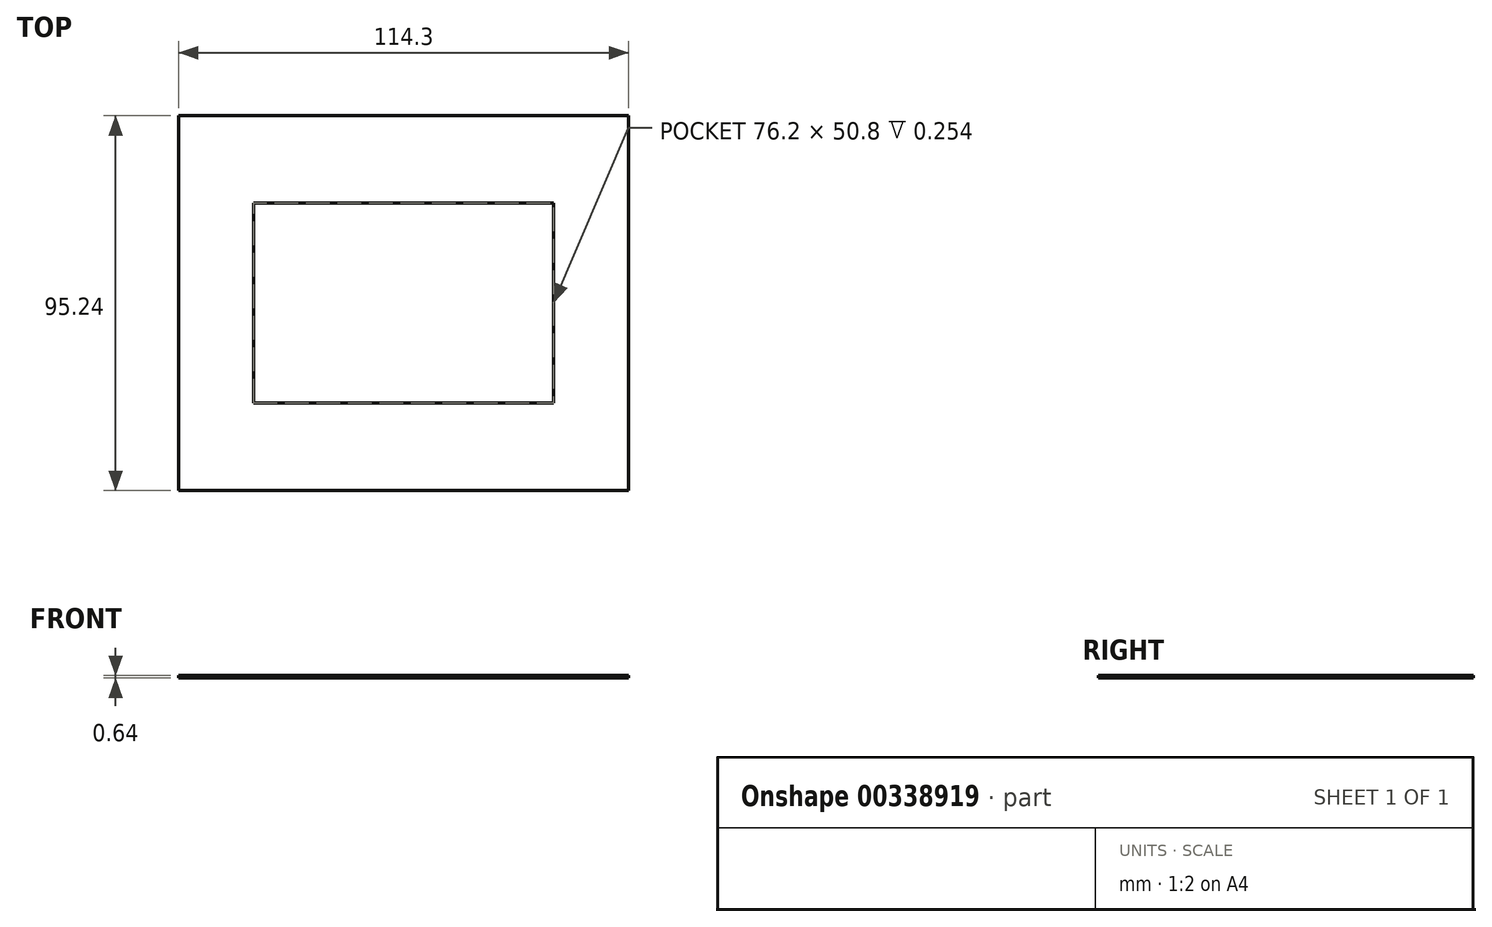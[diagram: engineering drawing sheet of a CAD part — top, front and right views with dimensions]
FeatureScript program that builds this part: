
annotation { "Feature Type Name" : "Feature", "Feature Type Description" : "" }
export const myFeature = defineFeature(function(context is Context, id is Id, definition is map)
    precondition{}
    {
        {
            var Q0;
            Q0=qCreatedBy(makeId("Top.planeOp"),FACE);
            var sketch = newSketch(context, id + "F0", { "sketchPlane" : qUnion([Q0])});
            skLineSegment(sketch, "E0.bottom", {"start": v(57.15, 47.62) * mm, "end": v(-57.15, 47.63) * mm});
            skLineSegment(sketch, "E0.top", {"start": v(57.15, -47.62) * mm, "end": v(-57.15, -47.62) * mm});
            skLineSegment(sketch, "E0.left", {"start": v(57.15, 47.62) * mm, "end": v(57.15, -47.63) * mm});
            skLineSegment(sketch, "E0.right", {"start": v(-57.15, 47.63) * mm, "end": v(-57.15, -47.63) * mm});
            skPoint(sketch, "E0.middle", {"position": v(0, 0) * mm});
            skSolve(sketch);
        }
        {
            var Q0;
            Q0 = qSketchRegion(id + "F0", true);
            extrude(context, id + "F1", {"entities" : qUnion([Q0]), "depth" : 0.64 * mm});
        }
        {
            var Q0;
            Q0=makeQuery(id+"F1.opExtrude","CAP_FACE",FACE,{"disambiguationData":[OSD([sQuery(id+"F0.wireOp",EDGE,"E0.bottom"),sQuery(id+"F0.wireOp",EDGE,"E0.top"),sQuery(id+"F0.wireOp",EDGE,"E0.left"),sQuery(id+"F0.wireOp",EDGE,"E0.right")])],"isStart":false});
            var sketch = newSketch(context, id + "F2", { "sketchPlane" : qUnion([Q0])});
            skLineSegment(sketch, "E1.bottom", {"start": v(38.1, 25.4) * mm, "end": v(-38.1, 25.4) * mm});
            skLineSegment(sketch, "E1.top", {"start": v(38.1, -25.4) * mm, "end": v(-38.1, -25.4) * mm});
            skLineSegment(sketch, "E1.left", {"start": v(38.1, 25.4) * mm, "end": v(38.1, -25.4) * mm});
            skLineSegment(sketch, "E1.right", {"start": v(-38.1, 25.4) * mm, "end": v(-38.1, -25.4) * mm});
            skPoint(sketch, "E1.middle", {"position": v(0, 0) * mm});
            skSolve(sketch);
        }
        {
            var Q0;
            Q0 = qSketchRegion(id + "F2", true);
            var Q1;
            Q1 = qSketchRegion(id + "F0", true);
            extrude(context, id + "F3", {"entities" : qUnion([Q0, Q1]), "operationType" : NewBodyOperationType.REMOVE, "oppositeDirection" : true, "depth" : 0.25 * mm});
        }
    });
